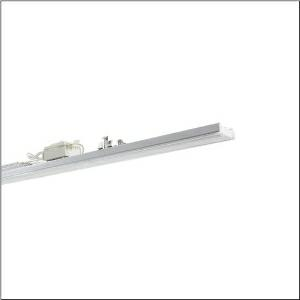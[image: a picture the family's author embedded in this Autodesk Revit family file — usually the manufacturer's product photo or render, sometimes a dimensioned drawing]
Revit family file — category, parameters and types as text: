
# Revit family: licross_11_recessed_ho_51tl12mn46xm
name_source: partatom
category: Lighting Fixtures
units: mm (PartAtom-declared; Revit-internal decimal feet)

## family parameters
Cut with Voids When Loaded = No
Host = Face
Light Source = No
Part Type = Normal
Room Calculation Point = No
Round Connector Dimension = Use Diameter
Shared = No

## types (1)
- --- (1 x LED, 6020 lm, 30.1 W, 4000K)
    Apparent Load = 30 VA
    CIE Flux Codes = 66 91 98 100 100
    Color Rendering = 80
    Color Temperature = 4000K
    Default Elevation = 1800 mm
    Description = Licross 11 Recessed HO, luminaire insert, of sheet steel, coil coated, white, length: 1.500mm, width: 66mm, height: 67mm, LED rated luminous flux: 6.020lm, light colour: 840, SDCM (Standard Deviation of Colour Matching)MacAdam ≤ 2 SDCM (initial), control gear: ON/OFF Multilumen, with plug, 3-pole, with phase selection, mains connection: 220..240V, AC, 50/60Hz, rated input power: 30W, internal wiring halogen-free, primary optical cover: cover, of PMMA, light emission: direct distribution, primary light characteristic: symmetric, protection rating (complete): IP40, insulation class (complete): insulation class I (protective earthing), certification: CE, ENEC, VDE, UKCA, protection symbol: D if used in an environment without relevant dust loads with corresponding accessories, impact resistance: IK06, permissible ambient temperature for indoor applications: -35..+50°C, corresponds to IFS (International Featured Standards) requirements for safety and quality in the food industry, reducing of maximum allowable ambient temperature of 5°C with ceiling mounting, The light source and the operating device comply with the requirements of the Ecodesign Regulation (EU) 2019/2020 and are replaceable in accordance with this regulation, packaging unit: 1 piece
    Height = 58 mm
    Lamp = 1 x LED
    Lamp Light Flux = 6020 lm
    Lamp Power = 30.1 W
    Lamp count = 1
    Length = 1500 mm
    Luminous efficacy = 200 lm/W
    Manufacturer = Siteco
    ModVariant = No
    Model = 51TL12MN46XM
    Mounting Place = Ceiling
    Mounting Type = Pendant
    Number of Poles = 1
    OnlyDefault = Yes
    Power Factor = 1
    Product Name = Licross 11 Recessed HO
    Product group = luminaire insert | ceiling pendant
    ProductGroupID = 901
    Protection Class = Protection class I
    Protection Degree = IP 40
    RLX_Detail_Level = 1
    RLX_Emergency_Light_Flux = 0 lm
    RLX_Emergency_Type = 0
    RLX_Emergency_Type_DB = No
    RlxData = <blob elided: 22277 chars, md5=9824c000>
    Socket = socket
    Standby Power = 0 W
    System Light Flux = 6020 lm
    System Power = 30 W
    Type Comments = factory setting: luminous flux: 100 % | (A | C | E) | 71 mA
    Type Image = l_1296930.jpg
    URL = http://relux.com
    VarID = @adj_089599
    Voltage = 0 V
    Weight = 0.00 kg
    Width = 66 mm

## geometry (parser evidence)
native form markers: Blend x4, Sweep x11
no freeform markers — native parametric forms only
